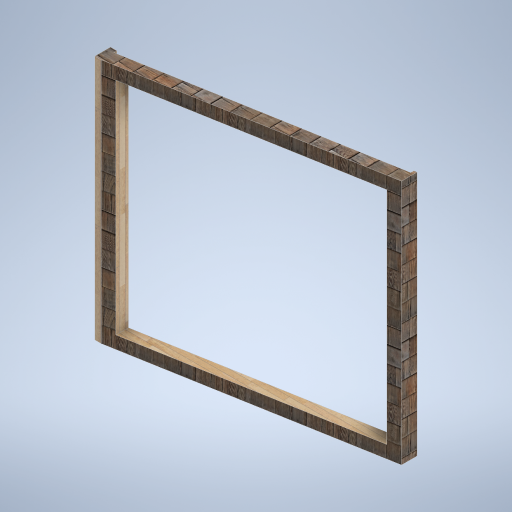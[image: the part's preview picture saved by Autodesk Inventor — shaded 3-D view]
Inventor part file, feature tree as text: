
AUTODESK INVENTOR PART (.ipt)
format: ipt  version: 2024.2 (Build 282272000, 272)  size: 400,896 bytes
history: native  units: mm
features: sketch x7, plane x4, extrude x3, projected_geometry x2, loft x1, other x1
ambient origin geometry x8: Origin, YZ Plane, XZ Plane, XY Plane, X Axis, Y Axis, Z Axis, Center Point
bodies: Solid1 (feature_tree)
feature tree (18):
  sketch  "Sketch1"  dims[d0=0.0mm d1=2500.0mm d2=150.0mm]
  plane  "Work Plane2"
  extrude  "Extrusion1"  Depth=150.0mm
  plane  "Work Plane3"
  sketch  "Sketch3"  dims[d3=60.0mm d4=0.0mm d5=0.0mm]
  sketch  "Sketch5"  dims[d6=13.962634mm d7=13.962634mm]
  plane  "Work Plane4"
  sketch  "Sketch6"  dims[d12=0.0mm d13=90.0deg d14=0.0mm d15=90.0deg]
  loft  "Loft2"
  extrude  "Extrusion2"  Depth=13.962634mm
  extrude  "Extrusion3"  TaperAngle=0.0deg  [1 undecoded]
  plane  "Work Plane1"
  projected_geometry  "Projected Loop1"
  sketch  "Sketch9"  dims[d16=30.0mm]
  other  "Edges2"
  sketch  "Sketch10"  dims[d17=2450.0mm]
  sketch  "Sketch11"  dims[d18=1.745329mm d19=2450.0mm d20=0.0mm d21=0.0mm d22=120.0mm d23=120.0mm d24=120.0mm d25=120.0mm d26=0.0mm d27=0.0mm]
  projected_geometry  "Projected Loop2"
note: 1 required parameter value undecoded (feature->parameter linkage not recoverable at this tier; creation-order binding heuristic only, values carry confidence <= 0.55)
